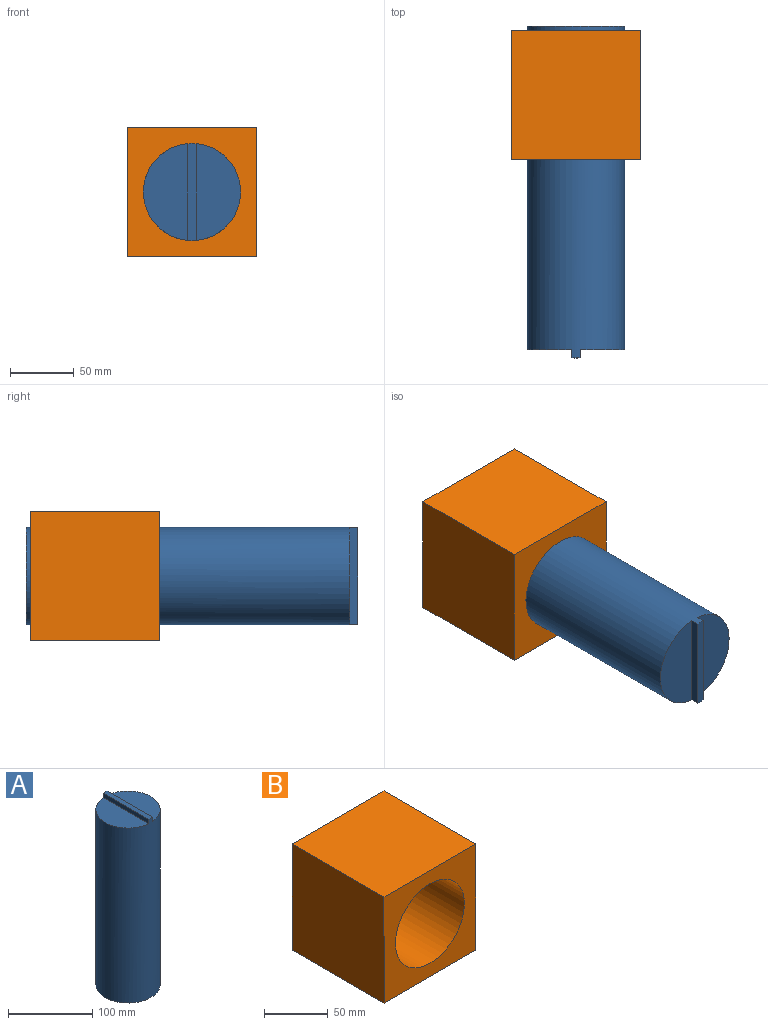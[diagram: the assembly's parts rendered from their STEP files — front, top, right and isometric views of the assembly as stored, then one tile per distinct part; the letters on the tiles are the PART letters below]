
ASSEMBLY  parts=2 mates=1
PART A: 7 faces, bbox 76.2x76.2x260.4 mm
  f0: plane 75.94x34.93mm, normal (0,0,1), area 2038.5mm2, adj f1,f5
  f1: cylinder r=38.1mm len=260.35mm, axis (0,0,-1), area 60885.6mm2, adj f0,f2,f3,f4,f5,f6
  f2: plane 75.94x34.93mm, normal (0,0,1), area 2038.5mm2, adj f1,f4
  f3: plane 76.2x76.2mm, normal (0,0,-1), area 4560.4mm2, adj f1
  f4: plane 75.94x6.35mm, normal (-1,0,0), area 482.2mm2, adj f1,f2,f6
  f5: plane 75.94x6.35mm, normal (1,0,0), area 482.2mm2, adj f0,f1,f6
  f6: plane 76.2x6.35mm, normal (0,0,1), area 483.3mm2, adj f1,f4,f5
PART B: 7 faces, bbox 101.6x101.6x101.6 mm
  f0: plane 101.6x101.6mm, normal (-1,0,0), area 10322.6mm2, adj f1,f3,f5,f6
  f1: plane 101.6x101.6mm, normal (0,0,-1), area 10322.6mm2, adj f0,f2,f5,f6
  f2: plane 101.6x101.6mm, normal (1,0,0), area 10322.6mm2, adj f1,f3,f5,f6
  f3: plane 101.6x101.6mm, normal (0,0,1), area 10322.6mm2, adj f0,f2,f5,f6
  f4: cylinder r=38.1mm len=101.6mm, axis (0,1,0), area 24322mm2, adj f5,f6
  f5: plane 101.6x101.6mm, normal (0,-1,0), area 5762.2mm2, adj f0,f1,f2,f3,f4
  f6: plane 101.6x101.6mm, normal (0,1,0), area 5762.2mm2, adj f0,f1,f2,f3,f4
PLACE A rot(axis=(1,0,0),90deg) t=(0,53.97,50.8)mm
PLACE B t=(-50.8,50.8,0)mm
MATE slider A.f1 <-> B.f4  axis (0,1,0) through (0,-76.2,50.8)mm
